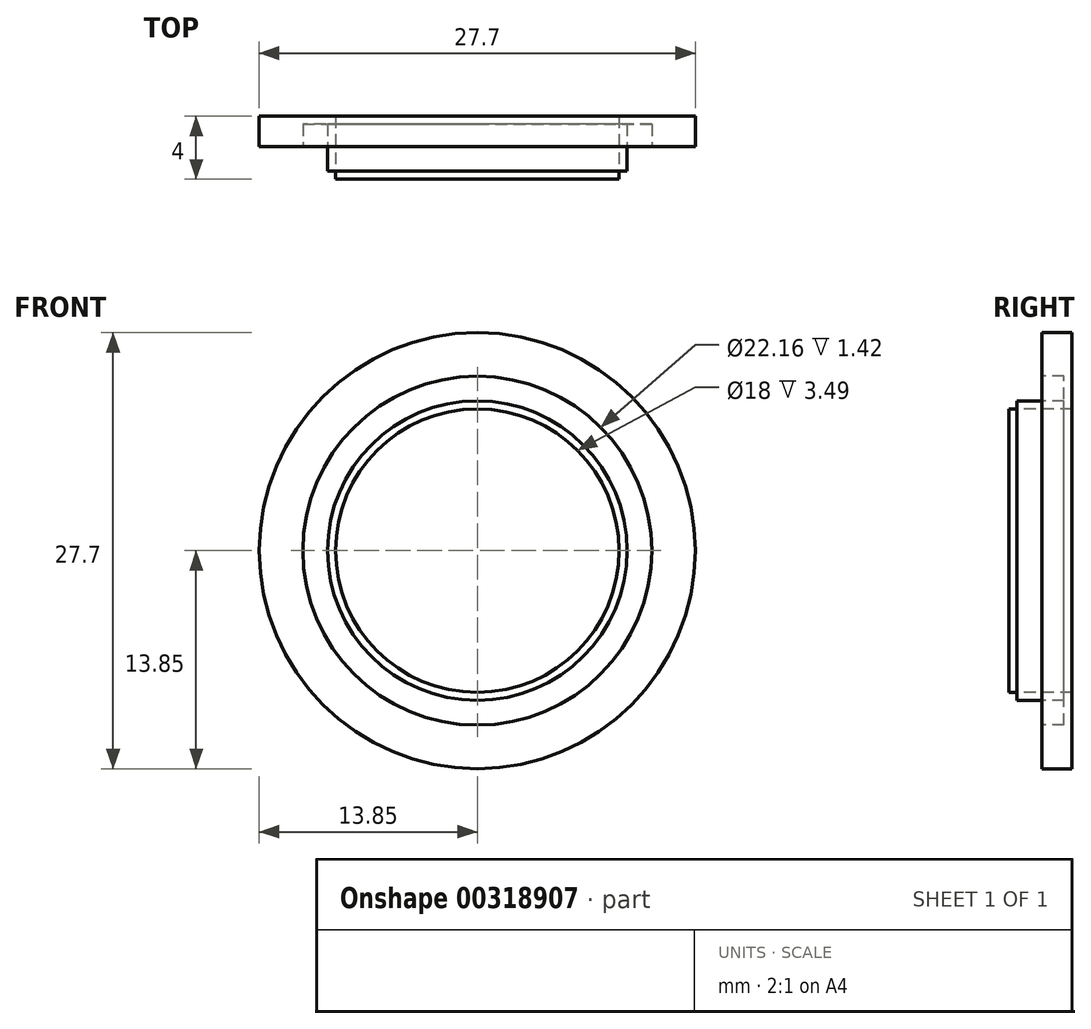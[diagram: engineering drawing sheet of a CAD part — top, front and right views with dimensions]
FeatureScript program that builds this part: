
annotation { "Feature Type Name" : "Feature", "Feature Type Description" : "" }
export const myFeature = defineFeature(function(context is Context, id is Id, definition is map)
    precondition{}
    {
        {
            var Q0;
            Q0=qCreatedBy(makeId("Top.planeOp"),FACE);
            var sketch = newSketch(context, id + "F0", { "sketchPlane" : qUnion([Q0])});
            skLineSegment(sketch, "E0", {"start": v(0, 0) * mm, "end": v(0, 3.5) * mm});
            skLineSegment(sketch, "E1", {"start": v(0, 3.5) * mm, "end": v(9.51, 3.5) * mm});
            skLineSegment(sketch, "E2", {"start": v(9.51, 3.5) * mm, "end": v(9.51, 0) * mm});
            skLineSegment(sketch, "E3", {"start": v(9.51, 0) * mm, "end": v(0, 0) * mm});
            skLineSegment(sketch, "E4", {"start": v(9.51, 0) * mm, "end": v(9, 0) * mm, "construction": true});
            skLineSegment(sketch, "E5", {"start": v(9, 0) * mm, "end": v(9, 3.5) * mm});
            skLineSegment(sketch, "E6", {"start": v(9, 3.5) * mm, "end": v(9.51, 3.5) * mm});
            skLineSegment(sketch, "E7", {"start": v(9.51, 3.5) * mm, "end": v(11.08, 3.5) * mm});
            skLineSegment(sketch, "E8", {"start": v(11.08, 3.5) * mm, "end": v(11.08, 2.98) * mm});
            skLineSegment(sketch, "E9", {"start": v(11.08, 2.98) * mm, "end": v(9.51, 2.98) * mm});
            skLineSegment(sketch, "E10", {"start": v(11.08, 3.5) * mm, "end": v(13.85, 3.5) * mm});
            skLineSegment(sketch, "E11", {"start": v(13.85, 3.5) * mm, "end": v(13.85, 1.56) * mm});
            skLineSegment(sketch, "E12", {"start": v(13.85, 1.56) * mm, "end": v(11.08, 1.56) * mm});
            skLineSegment(sketch, "E13", {"start": v(11.08, 1.56) * mm, "end": v(11.08, 3.5) * mm});
            skSolve(sketch);
        }
        {
            var Q0;
            {var subQ0=sQuery(id+"F0.wireOp",EDGE,"E2");Q0=makeQuery(id+"F0.imprint","IMPRINT",FACE,{"disambiguationData":[TD([[makeQuery(id+"F0.imprint","IMPRINT",EDGE,{"derivedFrom":subQ0}),-1.0]])]});}
            var Q1;
            {var subQ0=sQuery(id+"F0.wireOp",EDGE,"E7");Q1=makeQuery(id+"F0.imprint","IMPRINT",FACE,{"disambiguationData":[TD([[makeQuery(id+"F0.imprint","IMPRINT",EDGE,{"derivedFrom":subQ0}),-1.0]])]});}
            var Q2;
            {var subQ3=sQuery(id+"F0.wireOp",EDGE,"E10");Q2=makeQuery(id+"F0.imprint","IMPRINT",FACE,{"disambiguationData":[TD([[makeQuery(id+"F0.imprint","IMPRINT",EDGE,{"derivedFrom":subQ3}),-1.0]])]});}
            var Q3;
            Q3=sQuery(id+"F0.wireOp",EDGE,"E0");
            revolve(context, id + "F1", {"entities" : qUnion([Q0, Q1, Q2]), "axis" : qUnion([Q3]), "revolveType" : RevolveType.FULL});
        }
        {
            var Q0;
            Q0=makeQuery(id+"F1.opRevolve","SWEPT_FACE",FACE,{"disambiguationData":[OSD([sQuery(id+"F0.wireOp",EDGE,"E3")])]});
            cPlane(context, id + "F2", {"entities" : qUnion([Q0]), "cplaneType" : CPlaneType.OFFSET, "offset" : 0 * mm, "width" : 150 * mm, "height" : 150 * mm});
        }
        {
            var Q0;
            Q0=qCreatedBy(id+"F2.planeOp",FACE);
            var sketch = newSketch(context, id + "F3", { "sketchPlane" : qUnion([Q0])});
            skCircle(sketch, "E14", {"center": v(0, 0) * mm, "radius": 9 * mm});
            skSolve(sketch);
        }
        {
            var Q0;
            Q0=makeQuery(id+"F3.imprint","IMPRINT",FACE,{"disambiguationData":[TD([[makeQuery(id+"F3.imprint","IMPRINT",EDGE,{"derivedFrom":sQuery(id+"F3.wireOp",EDGE,"E14")}),1.0]])]});
            extrude(context, id + "F4", {"entities" : qUnion([Q0]), "operationType" : NewBodyOperationType.ADD, "depth" : 0.51 * mm});
        }
        {
            var Q0;
            Q0=makeQuery(id+"F4.opExtrude","CAP_EDGE",EDGE,{"disambiguationData":[OSD([sQuery(id+"F3.wireOp",EDGE,"E14")])],"isStart":false});
            var Q1;
            Q1=makeQuery(id+"F1.opRevolve","SWEPT_EDGE",EDGE,{"disambiguationData":[OSD([sQuery(id+"F0.wireOp",EDGE,"E2"),sQuery(id+"F0.wireOp",EDGE,"E3")])]});
            loft(context, id + "F5", {"bodyType" : ToolBodyType.SURFACE, "wireProfilesArray" : [{ "wireProfileEntities" : qUnion([Q0]) }, { "wireProfileEntities" : qUnion([Q1]) }]});
        }
    });
